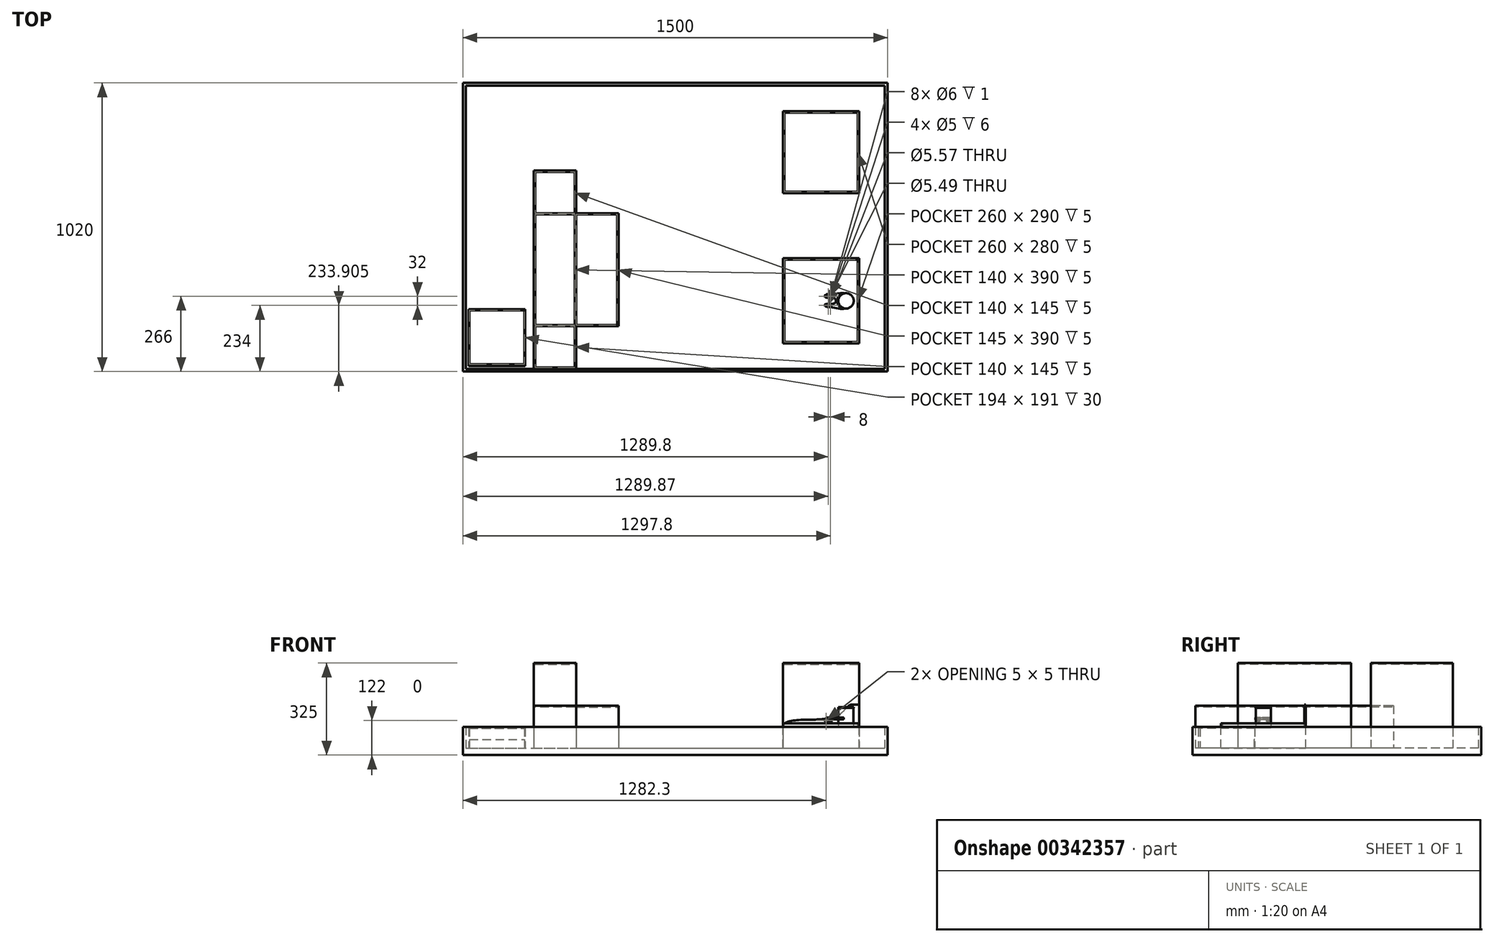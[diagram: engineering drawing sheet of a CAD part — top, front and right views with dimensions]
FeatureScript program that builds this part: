
annotation { "Feature Type Name" : "Feature", "Feature Type Description" : "" }
export const myFeature = defineFeature(function(context is Context, id is Id, definition is map)
    precondition{}
    {
        {
            var Q0;
            Q0=qCreatedBy(makeId("Top.planeOp"),FACE);
            var sketch = newSketch(context, id + "F0", { "sketchPlane" : qUnion([Q0])});
            skCircle(sketch, "E0", {"center": v(0, 0) * mm, "radius": 27.2 * mm});
            skSolve(sketch);
        }
        {
            var Q0;
            Q0=qSketchRegion(id+"F0",true);
            extrude(context, id + "F1", {"entities" : qUnion([Q0]), "depth" : 2.83 * mm});
        }
        {
            var Q0;
            Q0=makeQuery(id+"F1.opExtrude","CAP_FACE",FACE,{"disambiguationData":[OSD([sQuery(id+"F0.wireOp",EDGE,"E0")])],"isStart":false});
            var sketch = newSketch(context, id + "F2", { "sketchPlane" : qUnion([Q0])});
            skCircle(sketch, "E1", {"center": v(0, 0) * mm, "radius": 26.4 * mm});
            skSolve(sketch);
        }
        {
            var Q0;
            Q0=qSketchRegion(id+"F2",true);
            extrude(context, id + "F3", {"entities" : qUnion([Q0]), "operationType" : NewBodyOperationType.ADD, "depth" : 67.36 * mm});
        }
        {
            var Q0;
            Q0=makeQuery(id+"F3.opExtrude","CAP_FACE",FACE,{"disambiguationData":[OSD([sQuery(id+"F2.wireOp",EDGE,"E1")])],"isStart":false});
            var sketch = newSketch(context, id + "F4", { "sketchPlane" : qUnion([Q0])});
            skCircle(sketch, "E2", {"center": v(0, 0) * mm, "radius": 27.2 * mm});
            skSolve(sketch);
        }
        {
            var Q0;
            Q0=qSketchRegion(id+"F4",true);
            extrude(context, id + "F5", {"entities" : qUnion([Q0]), "operationType" : NewBodyOperationType.ADD, "depth" : 2.83 * mm});
        }
        {
            var Q0;
            Q0=makeQuery(id+"F5.opExtrude","CAP_FACE",FACE,{"disambiguationData":[OSD([sQuery(id+"F4.wireOp",EDGE,"E2")])],"isStart":false});
            var sketch = newSketch(context, id + "F6", { "sketchPlane" : qUnion([Q0])});
            skSolve(sketch);
        }
        {
            var Q0;
            Q0=qCreatedBy(makeId("Top.planeOp"),FACE);
            cPlane(context, id + "F7", {"entities" : qUnion([Q0]), "cplaneType" : CPlaneType.OFFSET, "offset" : 25 * mm, "width" : 150 * mm, "height" : 150 * mm});
        }
        {
            var Q0;
            Q0=makeQuery(id+"F6.imprint","IMPRINT",FACE,{"disambiguationData":[TD([[makeQuery(id+"F6.imprint","IMPRINT",EDGE,{"derivedFrom":makeQuery(id+"F5.opExtrude","CAP_EDGE",EDGE,{"disambiguationData":[OSD([sQuery(id+"F4.wireOp",EDGE,"E2")])],"isStart":false})}),1.0]])]});
            var sketch = newSketch(context, id + "F8", { "sketchPlane" : qUnion([Q0])});
            skSolve(sketch);
        }
        {
            var Q0;
            Q0=qCreatedBy(makeId("Top.planeOp"),FACE);
            var sketch = newSketch(context, id + "F9", { "sketchPlane" : qUnion([Q0])});
            skLineSegment(sketch, "E3.bottom", {"start": v(-222.8, -150) * mm, "end": v(47.2, -150) * mm});
            skLineSegment(sketch, "E3.top", {"start": v(-222.8, 150) * mm, "end": v(47.2, 150) * mm});
            skLineSegment(sketch, "E3.left", {"start": v(-222.8, -150) * mm, "end": v(-222.8, 150) * mm});
            skLineSegment(sketch, "E3.right", {"start": v(47.2, -150) * mm, "end": v(47.2, 150) * mm});
            skSolve(sketch);
        }
        {
            var Q0;
            Q0=qSketchRegion(id+"F9",true);
            extrude(context, id + "F10", {"entities" : qUnion([Q0]), "oppositeDirection" : true, "depth" : 72 * mm});
        }
        {
            var Q0;
            Q0=makeQuery(id+"F10.opExtrude","CAP_FACE",FACE,{"disambiguationData":[OSD([sQuery(id+"F9.wireOp",EDGE,"E3.bottom"),sQuery(id+"F9.wireOp",EDGE,"E3.top"),sQuery(id+"F9.wireOp",EDGE,"E3.left"),sQuery(id+"F9.wireOp",EDGE,"E3.right")])],"isStart":true});
            var sketch = newSketch(context, id + "F11", { "sketchPlane" : qUnion([Q0])});
            skLineSegment(sketch, "E4.bottom", {"start": v(-222.8, -150) * mm, "end": v(47.2, -150) * mm});
            skLineSegment(sketch, "E4.top", {"start": v(-222.8, -145) * mm, "end": v(42.2, -145) * mm});
            skLineSegment(sketch, "E4.left", {"start": v(-222.8, -150) * mm, "end": v(-222.8, -145) * mm});
            skLineSegment(sketch, "E5.bottom", {"start": v(47.2, 150) * mm, "end": v(42.2, 150) * mm});
            skLineSegment(sketch, "E5.left", {"start": v(47.2, 150) * mm, "end": v(47.2, -150) * mm});
            skLineSegment(sketch, "E5.right", {"start": v(42.2, 150) * mm, "end": v(42.2, -145) * mm});
            skSolve(sketch);
        }
        {
            var Q0;
            Q0=qSketchRegion(id+"F11",true);
            extrude(context, id + "F12", {"entities" : qUnion([Q0]), "operationType" : NewBodyOperationType.ADD, "depth" : 15 * mm});
        }
        {
            var Q0;
            Q0=makeQuery(id+"F12.boolean.opBoolean","MERGE",FACE,{"derivedFrom":[makeQuery(id+"F10.opExtrude","SWEPT_FACE",FACE,{"disambiguationData":[OSD([sQuery(id+"F9.wireOp",EDGE,"E3.top")])]}),makeQuery(id+"F12.opExtrude","SWEPT_FACE",FACE,{"disambiguationData":[OSD([sQuery(id+"F11.wireOp",EDGE,"E5.bottom")])]})]});
            var sketch = newSketch(context, id + "F13", { "sketchPlane" : qUnion([Q0])});
            skLineSegment(sketch, "E6", {"start": v(-47.2, 81.36) * mm, "end": v(-21.31, 81.36) * mm});
            skFitSpline(sketch, "E7", {"points": [v(-21.31, 81.36) * mm, v(15.24, 52.01) * mm, v(114.14, 28.17) * mm, v(222.8, 0) * mm], "startDerivative": vector(181.02, 0.3) * mm, "endDerivative": vector(-1.73, -239.85) * mm});
            skLineSegment(sketch, "E8", {"start": v(-47.2, 81.36) * mm, "end": v(-47.2, -72) * mm});
            skLineSegment(sketch, "E9", {"start": v(-47.2, -72) * mm, "end": v(222.8, -72) * mm});
            skLineSegment(sketch, "E10", {"start": v(222.8, -72) * mm, "end": v(222.8, 0) * mm});
            skSolve(sketch);
        }
        {
            var Q0;
            Q0=qSketchRegion(id+"F13",true);
            extrude(context, id + "F14", {"entities" : qUnion([Q0]), "operationType" : NewBodyOperationType.ADD, "oppositeDirection" : true, "depth" : 5 * mm});
        }
        {
            var Q0;
            Q0=makeQuery(id+"F10.opExtrude","CAP_FACE",FACE,{"disambiguationData":[OSD([sQuery(id+"F9.wireOp",EDGE,"E3.bottom"),sQuery(id+"F9.wireOp",EDGE,"E3.top"),sQuery(id+"F9.wireOp",EDGE,"E3.left"),sQuery(id+"F9.wireOp",EDGE,"E3.right")])],"isStart":true});
            var sketch = newSketch(context, id + "F15", { "sketchPlane" : qUnion([Q0])});
            skLineSegment(sketch, "E11.bottom", {"start": v(-222.8, 145) * mm, "end": v(-217.8, 145) * mm});
            skLineSegment(sketch, "E11.top", {"start": v(-222.8, -145) * mm, "end": v(-217.8, -145) * mm});
            skLineSegment(sketch, "E11.left", {"start": v(-222.8, 145) * mm, "end": v(-222.8, -145) * mm});
            skLineSegment(sketch, "E11.right", {"start": v(-217.8, 145) * mm, "end": v(-217.8, -145) * mm});
            skSolve(sketch);
        }
        {
            var Q0;
            Q0=qSketchRegion(id+"F15",true);
            extrude(context, id + "F16", {"entities" : qUnion([Q0]), "operationType" : NewBodyOperationType.ADD, "depth" : 5 * mm});
        }
        {
            var Q0;
            Q0=makeQuery(id+"F10.opExtrude","CAP_FACE",FACE,{"disambiguationData":[OSD([sQuery(id+"F9.wireOp",EDGE,"E3.bottom"),sQuery(id+"F9.wireOp",EDGE,"E3.top"),sQuery(id+"F9.wireOp",EDGE,"E3.left"),sQuery(id+"F9.wireOp",EDGE,"E3.right")])],"isStart":false});
            var sketch = newSketch(context, id + "F17", { "sketchPlane" : qUnion([Q0])});
            skLineSegment(sketch, "E12.bottom", {"start": v(147.2, 250) * mm, "end": v(-1352.8, 250) * mm});
            skLineSegment(sketch, "E12.top", {"start": v(147.2, -770) * mm, "end": v(-1352.8, -770) * mm});
            skLineSegment(sketch, "E12.left", {"start": v(147.2, 250) * mm, "end": v(147.2, -770) * mm});
            skLineSegment(sketch, "E12.right", {"start": v(-1352.8, 250) * mm, "end": v(-1352.8, -770) * mm});
            skSolve(sketch);
        }
        {
            var Q0;
            Q0=qSketchRegion(id+"F17",true);
            extrude(context, id + "F18", {"entities" : qUnion([Q0]), "operationType" : NewBodyOperationType.ADD, "depth" : 25 * mm});
        }
        {
            var Q0;
            Q0=makeQuery(id+"F18.opExtrude","CAP_FACE",FACE,{"disambiguationData":[OSD([sQuery(id+"F17.wireOp",EDGE,"E12.bottom"),sQuery(id+"F17.wireOp",EDGE,"E12.top"),sQuery(id+"F17.wireOp",EDGE,"E12.left"),sQuery(id+"F17.wireOp",EDGE,"E12.right")])],"isStart":true});
            var sketch = newSketch(context, id + "F19", { "sketchPlane" : qUnion([Q0])});
            skLineSegment(sketch, "E13.bottom", {"start": v(-222.8, 670) * mm, "end": v(47.2, 670) * mm});
            skLineSegment(sketch, "E13.top", {"start": v(-222.8, 380) * mm, "end": v(47.2, 380) * mm});
            skLineSegment(sketch, "E13.left", {"start": v(-222.8, 670) * mm, "end": v(-222.8, 380) * mm});
            skLineSegment(sketch, "E13.right", {"start": v(47.2, 670) * mm, "end": v(47.2, 380) * mm});
            skSolve(sketch);
        }
        {
            var Q0;
            Q0=qSketchRegion(id+"F19",true);
            extrude(context, id + "F20", {"entities" : qUnion([Q0]), "operationType" : NewBodyOperationType.ADD, "depth" : 300 * mm});
        }
        {
            var Q0;
            Q0=makeQuery(id+"F20.opExtrude","CAP_FACE",FACE,{"disambiguationData":[OSD([sQuery(id+"F19.wireOp",EDGE,"E13.bottom"),sQuery(id+"F19.wireOp",EDGE,"E13.top"),sQuery(id+"F19.wireOp",EDGE,"E13.left"),sQuery(id+"F19.wireOp",EDGE,"E13.right")])],"isStart":false});
            var sketch = newSketch(context, id + "F21", { "sketchPlane" : qUnion([Q0])});
            skLineSegment(sketch, "E14.bottom", {"start": v(-217.8, 665) * mm, "end": v(42.2, 665) * mm});
            skLineSegment(sketch, "E14.top", {"start": v(-217.8, 385) * mm, "end": v(42.2, 385) * mm});
            skLineSegment(sketch, "E14.left", {"start": v(-217.8, 665) * mm, "end": v(-217.8, 385) * mm});
            skLineSegment(sketch, "E14.right", {"start": v(42.2, 665) * mm, "end": v(42.2, 385) * mm});
            skSolve(sketch);
        }
        {
            var Q0;
            Q0=qSketchRegion(id+"F21",true);
            extrude(context, id + "F22", {"entities" : qUnion([Q0]), "operationType" : NewBodyOperationType.REMOVE, "oppositeDirection" : true, "depth" : 5 * mm});
        }
        {
            var Q0;
            Q0=makeQuery(id+"F18.opExtrude","CAP_FACE",FACE,{"disambiguationData":[OSD([sQuery(id+"F17.wireOp",EDGE,"E12.bottom"),sQuery(id+"F17.wireOp",EDGE,"E12.top"),sQuery(id+"F17.wireOp",EDGE,"E12.left"),sQuery(id+"F17.wireOp",EDGE,"E12.right")])],"isStart":true});
            var sketch = newSketch(context, id + "F23", { "sketchPlane" : qUnion([Q0])});
            skLineSegment(sketch, "E15.bottom", {"start": v(-1352.8, 770) * mm, "end": v(147.2, 770) * mm});
            skLineSegment(sketch, "E15.top", {"start": v(-1352.8, -250) * mm, "end": v(147.2, -250) * mm});
            skLineSegment(sketch, "E15.left", {"start": v(-1352.8, 770) * mm, "end": v(-1352.8, -250) * mm});
            skLineSegment(sketch, "E15.right", {"start": v(147.2, 770) * mm, "end": v(147.2, -250) * mm});
            skLineSegment(sketch, "E16.bottom", {"start": v(-1342.8, 760) * mm, "end": v(137.2, 760) * mm});
            skLineSegment(sketch, "E16.top", {"start": v(-1342.8, -240) * mm, "end": v(137.2, -240) * mm});
            skLineSegment(sketch, "E16.left", {"start": v(-1342.8, 760) * mm, "end": v(-1342.8, -240) * mm});
            skLineSegment(sketch, "E16.right", {"start": v(137.2, 760) * mm, "end": v(137.2, -240) * mm});
            skSolve(sketch);
        }
        {
            var Q0;
            Q0=qSketchRegion(id+"F23",true);
            extrude(context, id + "F24", {"entities" : qUnion([Q0]), "operationType" : NewBodyOperationType.ADD, "depth" : 75 * mm});
        }
        {
            var Q0;
            Q0=makeQuery(id+"F18.opExtrude","CAP_FACE",FACE,{"disambiguationData":[OSD([sQuery(id+"F17.wireOp",EDGE,"E12.bottom"),sQuery(id+"F17.wireOp",EDGE,"E12.top"),sQuery(id+"F17.wireOp",EDGE,"E12.left"),sQuery(id+"F17.wireOp",EDGE,"E12.right")])],"isStart":true});
            var sketch = newSketch(context, id + "F25", { "sketchPlane" : qUnion([Q0])});
            skLineSegment(sketch, "E17.bottom", {"start": v(-1102.8, 460) * mm, "end": v(-952.8, 460) * mm});
            skLineSegment(sketch, "E17.top", {"start": v(-1102.8, -240) * mm, "end": v(-952.8, -240) * mm});
            skLineSegment(sketch, "E17.left", {"start": v(-1102.8, 460) * mm, "end": v(-1102.8, -240) * mm});
            skLineSegment(sketch, "E17.right", {"start": v(-952.8, 460) * mm, "end": v(-952.8, 310) * mm});
            skLineSegment(sketch, "E18.bottom", {"start": v(-952.8, 310) * mm, "end": v(-802.8, 310) * mm});
            skLineSegment(sketch, "E18.top", {"start": v(-952.8, -90) * mm, "end": v(-802.8, -90) * mm});
            skLineSegment(sketch, "E18.right", {"start": v(-802.8, 310) * mm, "end": v(-802.8, -90) * mm});
            skLineSegment(sketch, "E19.trimOffspring", {"start": v(-952.8, -90) * mm, "end": v(-952.8, -240) * mm});
            skSolve(sketch);
        }
        {
            var Q0;
            Q0=qSketchRegion(id+"F25",true);
            extrude(context, id + "F26", {"entities" : qUnion([Q0]), "operationType" : NewBodyOperationType.ADD, "depth" : 150 * mm});
        }
        {
            var Q0;
            Q0=makeQuery(id+"F26.opExtrude","CAP_FACE",FACE,{"disambiguationData":[OSD([sQuery(id+"F25.wireOp",EDGE,"E17.bottom"),sQuery(id+"F25.wireOp",EDGE,"E17.top"),sQuery(id+"F25.wireOp",EDGE,"E17.left"),sQuery(id+"F25.wireOp",EDGE,"E17.right"),sQuery(id+"F25.wireOp",EDGE,"E18.bottom"),sQuery(id+"F25.wireOp",EDGE,"E18.top"),sQuery(id+"F25.wireOp",EDGE,"E18.right"),sQuery(id+"F25.wireOp",EDGE,"E19.trimOffspring")])],"isStart":false});
            var sketch = newSketch(context, id + "F27", { "sketchPlane" : qUnion([Q0])});
            skLineSegment(sketch, "E20.bottom", {"start": v(-952.8, 310) * mm, "end": v(-1102.8, 310) * mm});
            skLineSegment(sketch, "E20.top", {"start": v(-952.8, -90) * mm, "end": v(-1102.8, -90) * mm});
            skLineSegment(sketch, "E20.left", {"start": v(-952.8, 310) * mm, "end": v(-952.8, -90) * mm});
            skLineSegment(sketch, "E20.right", {"start": v(-1102.8, 310) * mm, "end": v(-1102.8, -90) * mm});
            skSolve(sketch);
        }
        {
            var Q0;
            Q0=qSketchRegion(id+"F27",true);
            extrude(context, id + "F28", {"entities" : qUnion([Q0]), "operationType" : NewBodyOperationType.ADD, "depth" : 150 * mm});
        }
        {
            var Q0;
            Q0=makeQuery(id+"F28.opExtrude","CAP_FACE",FACE,{"disambiguationData":[OSD([sQuery(id+"F27.wireOp",EDGE,"E20.bottom"),sQuery(id+"F27.wireOp",EDGE,"E20.top"),sQuery(id+"F27.wireOp",EDGE,"E20.left"),sQuery(id+"F27.wireOp",EDGE,"E20.right")])],"isStart":false});
            var sketch = newSketch(context, id + "F29", { "sketchPlane" : qUnion([Q0])});
            skLineSegment(sketch, "E21.bottom", {"start": v(-1097.8, 305) * mm, "end": v(-957.8, 305) * mm});
            skLineSegment(sketch, "E21.top", {"start": v(-1097.8, -85) * mm, "end": v(-957.8, -85) * mm});
            skLineSegment(sketch, "E21.left", {"start": v(-1097.8, 305) * mm, "end": v(-1097.8, -85) * mm});
            skLineSegment(sketch, "E21.right", {"start": v(-957.8, 305) * mm, "end": v(-957.8, -85) * mm});
            skSolve(sketch);
        }
        {
            var Q0;
            Q0=qSketchRegion(id+"F29",true);
            extrude(context, id + "F30", {"entities" : qUnion([Q0]), "operationType" : NewBodyOperationType.REMOVE, "oppositeDirection" : true, "depth" : 5 * mm});
        }
        {
            var Q0;
            {var subQ0=sQuery(id+"F25.wireOp",EDGE,"E17.left");var subQ1=sQuery(id+"F25.wireOp",EDGE,"E18.bottom");var subQ2=sQuery(id+"F25.wireOp",EDGE,"E17.right");var subQ3=sQuery(id+"F25.wireOp",EDGE,"E17.bottom");var subQ4=makeQuery(id+"F26.opExtrude","CAP_FACE",FACE,{"disambiguationData":[OSD([subQ3,sQuery(id+"F25.wireOp",EDGE,"E17.top"),subQ0,subQ2,subQ1,sQuery(id+"F25.wireOp",EDGE,"E18.top"),sQuery(id+"F25.wireOp",EDGE,"E18.right"),sQuery(id+"F25.wireOp",EDGE,"E19.trimOffspring")])],"isStart":false});Q0=makeQuery(id+"F28.boolean.opBoolean","SPLIT",FACE,{"disambiguationData":[TD([makeQuery(id+"F26.opExtrude","SWEPT_FACE",FACE,{"disambiguationData":[OSD([subQ3])]})])],"derivedFrom":subQ4});}
            var sketch = newSketch(context, id + "F31", { "sketchPlane" : qUnion([Q0])});
            skLineSegment(sketch, "E22.bottom", {"start": v(-1097.8, 455) * mm, "end": v(-957.8, 455) * mm});
            skLineSegment(sketch, "E22.top", {"start": v(-1097.8, 310) * mm, "end": v(-957.8, 310) * mm});
            skLineSegment(sketch, "E22.left", {"start": v(-1097.8, 455) * mm, "end": v(-1097.8, 310) * mm});
            skLineSegment(sketch, "E22.right", {"start": v(-957.8, 455) * mm, "end": v(-957.8, 310) * mm});
            skLineSegment(sketch, "E23.bottom", {"start": v(-952.8, 305) * mm, "end": v(-807.8, 305) * mm});
            skLineSegment(sketch, "E23.top", {"start": v(-952.8, -85) * mm, "end": v(-807.8, -85) * mm});
            skLineSegment(sketch, "E23.left", {"start": v(-952.8, 305) * mm, "end": v(-952.8, -85) * mm});
            skLineSegment(sketch, "E23.right", {"start": v(-807.8, 305) * mm, "end": v(-807.8, -85) * mm});
            skLineSegment(sketch, "E24.bottom", {"start": v(-1097.8, -90) * mm, "end": v(-957.8, -90) * mm});
            skLineSegment(sketch, "E24.top", {"start": v(-1097.8, -235) * mm, "end": v(-957.8, -235) * mm});
            skLineSegment(sketch, "E24.left", {"start": v(-1097.8, -90) * mm, "end": v(-1097.8, -235) * mm});
            skLineSegment(sketch, "E24.right", {"start": v(-957.8, -90) * mm, "end": v(-957.8, -235) * mm});
            skSolve(sketch);
        }
        {
            var Q0;
            Q0=qSketchRegion(id+"F31",true);
            extrude(context, id + "F32", {"entities" : qUnion([Q0]), "operationType" : NewBodyOperationType.REMOVE, "oppositeDirection" : true, "depth" : 5 * mm});
        }
        {
            var Q0;
            Q0=qCreatedBy(id+"F7.planeOp",FACE);
            var sketch = newSketch(context, id + "F33", { "sketchPlane" : qUnion([Q0])});
            skLineSegment(sketch, "E25", {"start": v(0, 0) * mm, "end": v(-90, 0) * mm, "construction": true});
            skLineSegment(sketch, "E26.bottom", {"start": v(-74.5, -12) * mm, "end": v(-55, -12) * mm});
            skLineSegment(sketch, "E26.top", {"start": v(-74.5, -20) * mm, "end": v(-55, -20) * mm});
            skLineSegment(sketch, "E26.left", {"start": v(-74.5, -12) * mm, "end": v(-74.5, -13) * mm});
            skPoint(sketch, "E27.visualSharp", {"position": v(-51, -12) * mm});
            skPoint(sketch, "E28.visualSharp", {"position": v(-51, -20) * mm});
            skCircle(sketch, "E29", {"center": v(-55, -16) * mm, "radius": 3 * mm});
            skLineSegment(sketch, "E30", {"start": v(-59, -3.98) * mm, "end": v(-59, -18.08) * mm, "construction": true});
            skCircle(sketch, "E31.MirrorC", {"center": v(-63, -16) * mm, "radius": 3 * mm});
            skLineSegment(sketch, "E32.bottom", {"start": v(-74.5, -13) * mm, "end": v(-65.65, -13) * mm});
            skLineSegment(sketch, "E32.top", {"start": v(-74.5, -19) * mm, "end": v(-65.65, -19) * mm});
            skArc(sketch, "E33", {"start": v(-65.65, -13) * mm, "mid": v(-67, -16) * mm, "end": v(-65.65, -19) * mm});
            skLineSegment(sketch, "E34.trimOffspring", {"start": v(-74.5, -19) * mm, "end": v(-74.5, -20) * mm});
            skArc(sketch, "E35.trimOffspring", {"start": v(-55, -20) * mm, "mid": v(-51, -16) * mm, "end": v(-55, -12) * mm});
            skLineSegment(sketch, "E36.MirrorCS", {"start": v(-74.5, 12) * mm, "end": v(-74.5, 13) * mm});
            skLineSegment(sketch, "E37.MirrorCS", {"start": v(-74.5, 19) * mm, "end": v(-74.5, 20) * mm});
            skPoint(sketch, "E38.MirrorP", {"position": v(-51, 12) * mm});
            skLineSegment(sketch, "E39.MirrorCS", {"start": v(-74.5, 12) * mm, "end": v(-55, 12) * mm});
            skPoint(sketch, "E40.MirrorP", {"position": v(-51, 20) * mm});
            skArc(sketch, "E41.MirrorCS", {"start": v(-65.65, 13) * mm, "mid": v(-67, 16) * mm, "end": v(-65.65, 19) * mm});
            skArc(sketch, "E42.MirrorCS", {"start": v(-55, 20) * mm, "mid": v(-51, 16) * mm, "end": v(-55, 12) * mm});
            skLineSegment(sketch, "E43.MirrorCS", {"start": v(-74.5, 20) * mm, "end": v(-55, 20) * mm});
            skCircle(sketch, "E44.MirrorC", {"center": v(-55, 16) * mm, "radius": 3 * mm});
            skCircle(sketch, "E45.MirrorC", {"center": v(-63, 16) * mm, "radius": 3 * mm});
            skLineSegment(sketch, "E46.MirrorCS", {"start": v(-74.5, 19) * mm, "end": v(-65.65, 19) * mm});
            skLineSegment(sketch, "E47.MirrorCS", {"start": v(-74.5, 13) * mm, "end": v(-65.65, 13) * mm});
            skSolve(sketch);
        }
        {
            var Q0;
            Q0=qSketchRegion(id+"F33",true);
            var Q1;
            Q1=qSketchRegion(id+"F36",true);
            extrude(context, id + "F34", {"entities" : qUnion([Q0, Q1]), "endBound" : BoundingType.SYMMETRIC, "depth" : 8 * mm});
        }
        {
            var Q0;
            Q0=makeQuery(id+"F34.opExtrude","CAP_EDGE",EDGE,{"disambiguationData":[OSD([sQuery(id+"F33.wireOp",EDGE,"E34.trimOffspring")])],"isStart":false});
            var Q1;
            Q1=makeQuery(id+"F34.opExtrude","CAP_EDGE",EDGE,{"disambiguationData":[OSD([sQuery(id+"F33.wireOp",EDGE,"E26.left")])],"isStart":false});
            var Q2;
            Q2=makeQuery(id+"F34.opExtrude","CAP_EDGE",EDGE,{"disambiguationData":[OSD([sQuery(id+"F33.wireOp",EDGE,"E34.trimOffspring")])],"isStart":true});
            var Q3;
            Q3=makeQuery(id+"F34.opExtrude","CAP_EDGE",EDGE,{"disambiguationData":[OSD([sQuery(id+"F33.wireOp",EDGE,"E26.left")])],"isStart":true});
            var Q4;
            Q4=makeQuery(id+"F34.opExtrude","CAP_EDGE",EDGE,{"disambiguationData":[OSD([sQuery(id+"F33.wireOp",EDGE,"E36.MirrorCS")])],"isStart":false});
            var Q5;
            Q5=makeQuery(id+"F34.opExtrude","CAP_EDGE",EDGE,{"disambiguationData":[OSD([sQuery(id+"F33.wireOp",EDGE,"E37.MirrorCS")])],"isStart":false});
            var Q6;
            Q6=makeQuery(id+"F34.opExtrude","CAP_EDGE",EDGE,{"disambiguationData":[OSD([sQuery(id+"F33.wireOp",EDGE,"E37.MirrorCS")])],"isStart":true});
            var Q7;
            Q7=makeQuery(id+"F34.opExtrude","CAP_EDGE",EDGE,{"disambiguationData":[OSD([sQuery(id+"F33.wireOp",EDGE,"E36.MirrorCS")])],"isStart":true});
            fillet(context, id + "F35", {"entities" : qUnion([Q0, Q1, Q2, Q3, Q4, Q5, Q6, Q7]), "radius" : 4 * mm, "tangentPropagation" : true, "allowEdgeOverflow" : false});
        }
        {
            var Q0;
            Q0=makeQuery(id+"F34.opExtrude","SWEPT_FACE",FACE,{"disambiguationData":[OSD([sQuery(id+"F33.wireOp",EDGE,"E26.top")])]});
            var sketch = newSketch(context, id + "F36", { "sketchPlane" : qUnion([Q0])});
            skCircle(sketch, "E48", {"center": v(-70.5, 25) * mm, "radius": 3 * mm});
            skSolve(sketch);
        }
        {
            var Q0;
            Q0=qSketchRegion(id+"F36",true);
            var Q1;
            Q1=makeQuery(id+"F34.opExtrude","SWEPT_FACE",FACE,{"disambiguationData":[OSD([sQuery(id+"F33.wireOp",EDGE,"E26.bottom")])]});
            extrude(context, id + "F37", {"entities" : qUnion([Q0]), "operationType" : NewBodyOperationType.ADD, "endBound" : BoundingType.UP_TO_SURFACE, "oppositeDirection" : true, "endBoundEntityFace" : qUnion([Q1]), "depth" : 25 * mm});
        }
        {
            var Q0;
            Q0=makeQuery(id+"F34.opExtrude","SWEPT_FACE",FACE,{"disambiguationData":[OSD([sQuery(id+"F33.wireOp",EDGE,"E43.MirrorCS")])]});
            var sketch = newSketch(context, id + "F38", { "sketchPlane" : qUnion([Q0])});
            skCircle(sketch, "E49", {"center": v(70.5, 25) * mm, "radius": 3 * mm});
            skSolve(sketch);
        }
        {
            var Q0;
            Q0=qSketchRegion(id+"F38",true);
            var Q1;
            Q1=makeQuery(id+"F34.opExtrude","SWEPT_FACE",FACE,{"disambiguationData":[OSD([sQuery(id+"F33.wireOp",EDGE,"E39.MirrorCS")])]});
            extrude(context, id + "F39", {"entities" : qUnion([Q0]), "operationType" : NewBodyOperationType.ADD, "endBound" : BoundingType.UP_TO_SURFACE, "oppositeDirection" : true, "endBoundEntityFace" : qUnion([Q1]), "depth" : 25 * mm});
        }
        {
            var Q0;
            Q0=qCreatedBy(id+"F7.planeOp",FACE);
            var sketch = newSketch(context, id + "F40", { "sketchPlane" : qUnion([Q0])});
            skCircle(sketch, "E50", {"center": v(-55, 16) * mm, "radius": 3 * mm});
            skCircle(sketch, "E51", {"center": v(-63, 16) * mm, "radius": 2.5 * mm});
            skCircle(sketch, "E52", {"center": v(-63, 16) * mm, "radius": 3 * mm});
            skCircle(sketch, "E53", {"center": v(-55, 16) * mm, "radius": 2.5 * mm});
            skSolve(sketch);
        }
        {
            var Q0;
            Q0=qSketchRegion(id+"F40",true);
            extrude(context, id + "F41", {"entities" : qUnion([Q0]), "operationType" : NewBodyOperationType.ADD, "endBound" : BoundingType.SYMMETRIC, "depth" : 6 * mm});
        }
        {
            var Q0;
            Q0=qCreatedBy(id+"F7.planeOp",FACE);
            var sketch = newSketch(context, id + "F42", { "sketchPlane" : qUnion([Q0])});
            skCircle(sketch, "E54", {"center": v(-63, -16) * mm, "radius": 2.5 * mm});
            skCircle(sketch, "E55", {"center": v(-63, -16) * mm, "radius": 3 * mm});
            skCircle(sketch, "E56", {"center": v(-55, -16) * mm, "radius": 2.5 * mm});
            skCircle(sketch, "E57", {"center": v(-55, -16) * mm, "radius": 3 * mm});
            skSolve(sketch);
        }
        {
            var Q0;
            Q0=qSketchRegion(id+"F42",true);
            extrude(context, id + "F43", {"entities" : qUnion([Q0]), "operationType" : NewBodyOperationType.ADD, "endBound" : BoundingType.SYMMETRIC, "depth" : 6 * mm});
        }
        {
            var Q0;
            Q0=makeQuery(id+"F34.opExtrude","SWEPT_FACE",FACE,{"disambiguationData":[OSD([sQuery(id+"F33.wireOp",EDGE,"E43.MirrorCS")])]});
            var sketch = newSketch(context, id + "F44", { "sketchPlane" : qUnion([Q0])});
            skArc(sketch, "E58", {"start": v(71.5, 27.3) * mm, "mid": v(70.5, 27.5) * mm, "end": v(69.5, 27.3) * mm});
            skLineSegment(sketch, "E59.bottom", {"start": v(68.2, 26) * mm, "end": v(69.5, 26) * mm});
            skLineSegment(sketch, "E59.top", {"start": v(68.2, 24) * mm, "end": v(69.5, 24) * mm});
            skLineSegment(sketch, "E60.left", {"start": v(71.5, 27.3) * mm, "end": v(71.5, 26) * mm});
            skLineSegment(sketch, "E60.right", {"start": v(69.5, 27.3) * mm, "end": v(69.5, 26) * mm});
            skPoint(sketch, "E61.orphan", {"position": v(69.5, 27.8) * mm});
            skPoint(sketch, "E62.orphan", {"position": v(71.5, 27.8) * mm});
            skArc(sketch, "E63.trimOffspring", {"start": v(68.2, 26) * mm, "mid": v(68, 25) * mm, "end": v(68.2, 24) * mm});
            skPoint(sketch, "E59.left.start.orphan", {"position": v(67.32, 26) * mm});
            skPoint(sketch, "E64.orphan", {"position": v(67.32, 24) * mm});
            skArc(sketch, "E65.trimOffspring", {"start": v(69.5, 22.7) * mm, "mid": v(70.5, 22.5) * mm, "end": v(71.5, 22.7) * mm});
            skLineSegment(sketch, "E66.trimOffspring", {"start": v(69.5, 24) * mm, "end": v(69.5, 22.7) * mm});
            skLineSegment(sketch, "E67.trimOffspring", {"start": v(71.5, 26) * mm, "end": v(72.8, 26) * mm});
            skLineSegment(sketch, "E68.trimOffspring", {"start": v(71.5, 24) * mm, "end": v(71.5, 22.7) * mm});
            skLineSegment(sketch, "E69.trimOffspring", {"start": v(71.5, 24) * mm, "end": v(72.8, 24) * mm});
            skPoint(sketch, "E60.top.end.orphan", {"position": v(69.5, 22.2) * mm});
            skPoint(sketch, "E70.orphan", {"position": v(71.5, 22.2) * mm});
            skPoint(sketch, "E59.right.end.orphan", {"position": v(73.68, 24) * mm});
            skPoint(sketch, "E71.orphan", {"position": v(73.68, 26) * mm});
            skArc(sketch, "E72.trimOffspring", {"start": v(72.8, 24) * mm, "mid": v(73, 25) * mm, "end": v(72.8, 26) * mm});
            skSolve(sketch);
        }
        {
            var Q0;
            Q0=qSketchRegion(id+"F44",true);
            extrude(context, id + "F45", {"entities" : qUnion([Q0]), "operationType" : NewBodyOperationType.REMOVE, "endBound" : BoundingType.THROUGH_ALL, "oppositeDirection" : true, "depth" : 25 * mm});
        }
        {
            var Q0;
            Q0=makeQuery(id+"F18.opExtrude","CAP_FACE",FACE,{"disambiguationData":[OSD([sQuery(id+"F17.wireOp",EDGE,"E12.bottom"),sQuery(id+"F17.wireOp",EDGE,"E12.top"),sQuery(id+"F17.wireOp",EDGE,"E12.left"),sQuery(id+"F17.wireOp",EDGE,"E12.right")])],"isStart":true});
            var sketch = newSketch(context, id + "F46", { "sketchPlane" : qUnion([Q0])});
            skLineSegment(sketch, "E73.bottom", {"start": v(-1332.8, -30) * mm, "end": v(-1132.8, -30) * mm});
            skLineSegment(sketch, "E73.top", {"start": v(-1332.8, -230) * mm, "end": v(-1132.8, -230) * mm});
            skLineSegment(sketch, "E73.left", {"start": v(-1332.8, -30) * mm, "end": v(-1332.8, -230) * mm});
            skLineSegment(sketch, "E73.right", {"start": v(-1132.8, -30) * mm, "end": v(-1132.8, -230) * mm});
            skLineSegment(sketch, "E74.bottom", {"start": v(-1329.8, -33) * mm, "end": v(-1135.8, -33) * mm});
            skLineSegment(sketch, "E74.top", {"start": v(-1329.8, -224) * mm, "end": v(-1135.8, -224) * mm});
            skLineSegment(sketch, "E74.left", {"start": v(-1329.8, -33) * mm, "end": v(-1329.8, -224) * mm});
            skLineSegment(sketch, "E74.right", {"start": v(-1135.8, -33) * mm, "end": v(-1135.8, -224) * mm});
            skSolve(sketch);
        }
        {
            var Q0;
            Q0=qSketchRegion(id+"F46",true);
            var Q1;
            Q1 = qSketchRegion(id + "F50", true);
            var Q2;
            Q2 = qSketchRegion(id + "FSVTdFIxLx9WnWu_5", true);
            extrude(context, id + "F47", {"entities" : qUnion([Q0, Q1, Q2]), "operationType" : NewBodyOperationType.ADD, "depth" : 30 * mm});
        }
        {
            var Q0;
            Q0=makeQuery(id+"F47.opExtrude","CAP_FACE",FACE,{"disambiguationData":[OSD([sQuery(id+"F46.wireOp",EDGE,"E73.bottom"),sQuery(id+"F46.wireOp",EDGE,"E73.top"),sQuery(id+"F46.wireOp",EDGE,"E73.left"),sQuery(id+"F46.wireOp",EDGE,"E73.right"),sQuery(id+"F46.wireOp",EDGE,"E74.bottom"),sQuery(id+"F46.wireOp",EDGE,"E74.top"),sQuery(id+"F46.wireOp",EDGE,"E74.left"),sQuery(id+"F46.wireOp",EDGE,"E74.right")])],"isStart":false});
            var sketch = newSketch(context, id + "F48", { "sketchPlane" : qUnion([Q0])});
            skLineSegment(sketch, "E75.bottom", {"start": v(-1332.8, -30) * mm, "end": v(-1329.8, -30) * mm});
            skLineSegment(sketch, "E75.top", {"start": v(-1332.8, -230) * mm, "end": v(-1329.8, -230) * mm});
            skLineSegment(sketch, "E75.left", {"start": v(-1332.8, -30) * mm, "end": v(-1332.8, -230) * mm});
            skLineSegment(sketch, "E75.right", {"start": v(-1329.8, -30) * mm, "end": v(-1329.8, -224) * mm});
            skLineSegment(sketch, "E76.bottom", {"start": v(-1329.8, -230) * mm, "end": v(-1135.8, -230) * mm});
            skLineSegment(sketch, "E76.top", {"start": v(-1329.8, -224) * mm, "end": v(-1135.8, -224) * mm});
            skLineSegment(sketch, "E77.bottom", {"start": v(-1135.8, -230) * mm, "end": v(-1132.8, -230) * mm});
            skLineSegment(sketch, "E77.top", {"start": v(-1135.8, -30) * mm, "end": v(-1132.8, -30) * mm});
            skLineSegment(sketch, "E77.left", {"start": v(-1135.8, -224) * mm, "end": v(-1135.8, -30) * mm});
            skLineSegment(sketch, "E77.right", {"start": v(-1132.8, -230) * mm, "end": v(-1132.8, -30) * mm});
            skSolve(sketch);
        }
        {
            var Q0;
            Q0=qSketchRegion(id+"F48",true);
            extrude(context, id + "F49", {"entities" : qUnion([Q0]), "operationType" : NewBodyOperationType.ADD, "depth" : 40 * mm});
        }
        {
            var Q0;
            Q0=makeQuery(id+"F34.opExtrude","CAP_FACE",FACE,{"disambiguationData":[OSD([sQuery(id+"F33.wireOp",EDGE,"E36.MirrorCS"),sQuery(id+"F33.wireOp",EDGE,"E37.MirrorCS"),sQuery(id+"F33.wireOp",EDGE,"E39.MirrorCS"),sQuery(id+"F33.wireOp",EDGE,"E41.MirrorCS"),sQuery(id+"F33.wireOp",EDGE,"E42.MirrorCS"),sQuery(id+"F33.wireOp",EDGE,"E43.MirrorCS"),sQuery(id+"F33.wireOp",EDGE,"E44.MirrorC"),sQuery(id+"F33.wireOp",EDGE,"E45.MirrorC"),sQuery(id+"F33.wireOp",EDGE,"E46.MirrorCS"),sQuery(id+"F33.wireOp",EDGE,"E47.MirrorCS")])],"isStart":false});
            var sketch = newSketch(context, id + "F50", { "sketchPlane" : qUnion([Q0])});
            skArc(sketch, "E78", {"start": v(-6.48, 27.12) * mm, "mid": v(-30.96, -0.03) * mm, "end": v(-7.57, -28.12) * mm});
            skLineSegment(sketch, "E79", {"start": v(-6.48, 27.12) * mm, "end": v(-19.08, 27.12) * mm});
            skLineSegment(sketch, "E80", {"start": v(-19.08, 27.12) * mm, "end": v(-53.3, 23.6) * mm});
            skLineSegment(sketch, "E81", {"start": v(-53.3, 23.6) * mm, "end": v(-66.5, 23.6) * mm});
            skLineSegment(sketch, "E82", {"start": v(-70.5, 19.6) * mm, "end": v(-70.5, 14.33) * mm});
            skLineSegment(sketch, "E83", {"start": v(-66.5, 10.33) * mm, "end": v(-45.6, 10.33) * mm});
            skPoint(sketch, "E84.end.orphan", {"position": v(-70.5, -12.78) * mm});
            skLineSegment(sketch, "E85", {"start": v(-66.5, -10.06) * mm, "end": v(-45.6, -10.06) * mm});
            skLineSegment(sketch, "E86", {"start": v(-35.6, -0.06) * mm, "end": v(-35.6, 0.33) * mm});
            skLineSegment(sketch, "E87", {"start": v(-70.5, -14.06) * mm, "end": v(-70.5, -17.48) * mm});
            skLineSegment(sketch, "E88", {"start": v(-66.5, -21.48) * mm, "end": v(-53.3, -21.48) * mm});
            skLineSegment(sketch, "E89", {"start": v(-53.3, -21.48) * mm, "end": v(-19.08, -28.28) * mm});
            skLineSegment(sketch, "E90", {"start": v(-19.08, -28.28) * mm, "end": v(-7.57, -28.12) * mm});
            skArc(sketch, "E91.filletArc", {"start": v(-35.6, 0.33) * mm, "mid": v(-38.53, 7.4) * mm, "end": v(-45.6, 10.33) * mm});
            skArc(sketch, "E92.filletArc", {"start": v(-45.6, -10.06) * mm, "mid": v(-38.53, -7.14) * mm, "end": v(-35.6, -0.06) * mm});
            skArc(sketch, "E93.filletArc", {"start": v(-66.5, 23.6) * mm, "mid": v(-69.33, 22.43) * mm, "end": v(-70.5, 19.6) * mm});
            skArc(sketch, "E94.filletArc", {"start": v(-70.5, 14.33) * mm, "mid": v(-69.33, 11.5) * mm, "end": v(-66.5, 10.33) * mm});
            skArc(sketch, "E95.filletArc", {"start": v(-66.5, -10.06) * mm, "mid": v(-69.33, -11.24) * mm, "end": v(-70.5, -14.06) * mm});
            skArc(sketch, "E96.filletArc", {"start": v(-70.5, -17.48) * mm, "mid": v(-69.33, -20.3) * mm, "end": v(-66.5, -21.48) * mm});
            skCircle(sketch, "E97", {"center": v(-63, 16) * mm, "radius": 2.71 * mm});
            skCircle(sketch, "E98", {"center": v(-55, 16) * mm, "radius": 2.75 * mm});
            skCircle(sketch, "E99", {"center": v(-55, -16) * mm, "radius": 2.67 * mm});
            skCircle(sketch, "E100", {"center": v(-62.93, -16.1) * mm, "radius": 2.78 * mm});
            skSolve(sketch);
        }
        {
            var Q0;
            Q0 = qSketchRegion(id + "F50", true);
            extrude(context, id + "F51", {"entities" : qUnion([Q0]), "depth" : 6 * mm});
        }
    });
